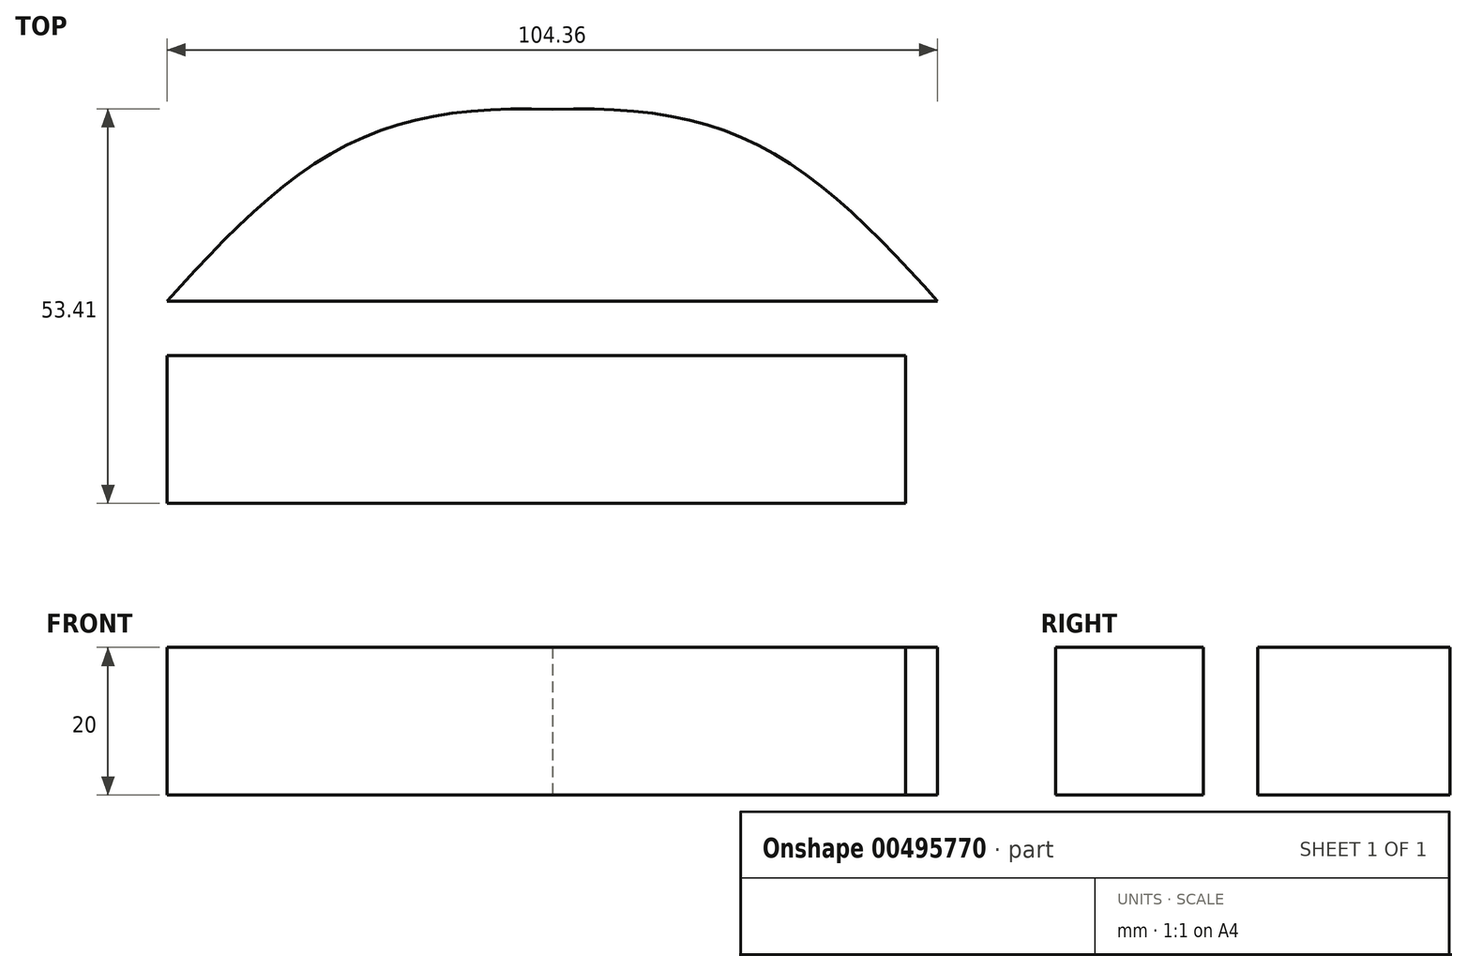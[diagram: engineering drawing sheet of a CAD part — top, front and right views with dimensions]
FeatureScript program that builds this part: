
annotation { "Feature Type Name" : "Feature", "Feature Type Description" : "" }
export const myFeature = defineFeature(function(context is Context, id is Id, definition is map)
    precondition{}
    {
        {
            var Q0;
            Q0=qCreatedBy(makeId("Top.planeOp"),FACE);
            var sketch = newSketch(context, id + "F0", { "sketchPlane" : qUnion([Q0])});
            skPoint(sketch, "E0.middle", {"position": v(0, 0) * mm});
            skPoint(sketch, "E1.2.internal.snap0", {"position": v(0, 10.44) * mm});
            skFitSpline(sketch, "E1", {"points": [v(-52.18, -10.44) * mm, v(-28.33, 10.44) * mm, v(0, 15.52) * mm], "startDerivative": vector(43.64, 48.53) * mm, "endDerivative": vector(66.6, -2.56) * mm});
            skLineSegment(sketch, "E2", {"start": v(0, 15.52) * mm, "end": v(0, -10.44) * mm});
            skLineSegment(sketch, "E3", {"start": v(-52.18, -10.44) * mm, "end": v(0, -10.44) * mm});
            skFitSpline(sketch, "E4.MirrorCS", {"points": [v(52.18, -10.44) * mm, v(28.33, 10.44) * mm, v(0, 15.52) * mm], "startDerivative": vector(-43.64, 48.53) * mm, "endDerivative": vector(-66.6, -2.56) * mm});
            skLineSegment(sketch, "E5.MirrorCS", {"start": v(52.18, -10.44) * mm, "end": v(0, -10.44) * mm});
            skLineSegment(sketch, "E6.bottom", {"start": v(-52.18, -17.81) * mm, "end": v(47.82, -17.81) * mm});
            skLineSegment(sketch, "E6.top", {"start": v(-52.18, -37.81) * mm, "end": v(47.82, -37.81) * mm});
            skLineSegment(sketch, "E6.left", {"start": v(-52.18, -17.81) * mm, "end": v(-52.18, -37.81) * mm});
            skLineSegment(sketch, "E6.right", {"start": v(47.82, -17.81) * mm, "end": v(47.82, -37.81) * mm});
            skSolve(sketch);
        }
        {
            var Q0;
            Q0=makeQuery(id+"F0.imprint","IMPRINT",FACE,{"disambiguationData":[TD([[makeQuery(id+"F0.imprint","IMPRINT",EDGE,{"derivedFrom":sQuery(id+"F0.wireOp",EDGE,"E1")}),-1.0]])]});
            var Q1;
            Q1=makeQuery(id+"F0.imprint","IMPRINT",FACE,{"disambiguationData":[TD([[makeQuery(id+"F0.imprint","IMPRINT",EDGE,{"derivedFrom":sQuery(id+"F0.wireOp",EDGE,"E2")}),1.0]])]});
            extrude(context, id + "F1", {"entities" : qUnion([Q0, Q1]), "depth" : 20 * mm});
        }
        {
            var Q0;
            Q0=makeQuery(id+"F0.imprint","IMPRINT",FACE,{"disambiguationData":[TD([[makeQuery(id+"F0.imprint","IMPRINT",EDGE,{"derivedFrom":sQuery(id+"F0.wireOp",EDGE,"E6.bottom")}),-1.0]])]});
            extrude(context, id + "F2", {"entities" : qUnion([Q0]), "depth" : 20 * mm});
        }
    });
